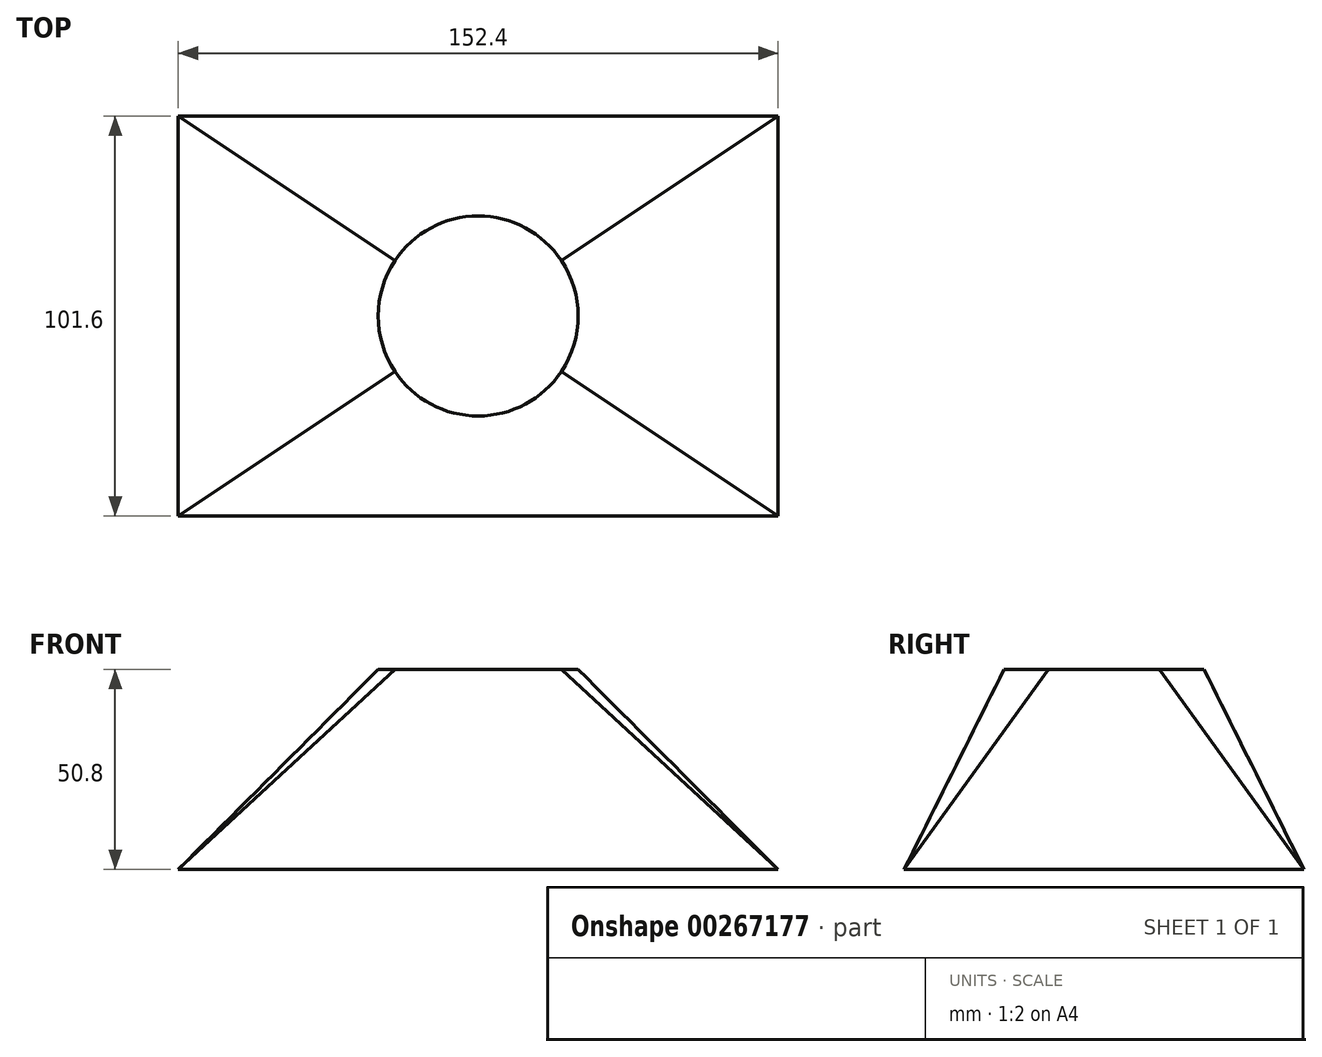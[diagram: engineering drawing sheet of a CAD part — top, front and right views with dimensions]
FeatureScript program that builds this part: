
annotation { "Feature Type Name" : "Feature", "Feature Type Description" : "" }
export const myFeature = defineFeature(function(context is Context, id is Id, definition is map)
    precondition{}
    {
        {
            var Q0;
            Q0=qCreatedBy(makeId("Top.planeOp"),FACE);
            var sketch = newSketch(context, id + "F0", { "sketchPlane" : qUnion([Q0])});
            skLineSegment(sketch, "E0.bottom", {"start": v(76.2, -50.8) * mm, "end": v(-76.2, -50.8) * mm});
            skLineSegment(sketch, "E0.top", {"start": v(76.2, 50.8) * mm, "end": v(-76.2, 50.8) * mm});
            skLineSegment(sketch, "E0.left", {"start": v(76.2, -50.8) * mm, "end": v(76.2, 50.8) * mm});
            skLineSegment(sketch, "E0.right", {"start": v(-76.2, -50.8) * mm, "end": v(-76.2, 50.8) * mm});
            skPoint(sketch, "E0.middle", {"position": v(0, 0) * mm});
            skSolve(sketch);
        }
        {
            var Q0;
            Q0=qCreatedBy(makeId("Top.planeOp"),FACE);
            cPlane(context, id + "F1", {"entities" : qUnion([Q0]), "cplaneType" : CPlaneType.OFFSET, "offset" : 50.8 * mm, "width" : 152.4 * mm, "height" : 152.4 * mm});
        }
        {
            var Q0;
            Q0=qCreatedBy(id+"F1.planeOp",FACE);
            var sketch = newSketch(context, id + "F2", { "sketchPlane" : qUnion([Q0])});
            skPoint(sketch, "E1.0", {"position": v(-76.2, 50.8) * mm});
            skPoint(sketch, "E2.0", {"position": v(76.2, 50.8) * mm});
            skPoint(sketch, "E3.0", {"position": v(76.2, -50.8) * mm});
            skPoint(sketch, "E4.0", {"position": v(-76.2, -50.8) * mm});
            skLineSegment(sketch, "E5", {"start": v(-76.2, 50.8) * mm, "end": v(21.13, -14.09) * mm, "construction": true});
            skLineSegment(sketch, "E6", {"start": v(76.2, 50.8) * mm, "end": v(-76.2, -50.8) * mm, "construction": true});
            skArc(sketch, "E7", {"start": v(-21.13, 14.09) * mm, "mid": v(-25.4, 0) * mm, "end": v(-21.13, -14.09) * mm});
            skArc(sketch, "E8", {"start": v(21.13, 14.09) * mm, "mid": v(0, 25.4) * mm, "end": v(-21.13, 14.09) * mm});
            skLineSegment(sketch, "E9", {"start": v(21.13, -14.09) * mm, "end": v(76.2, -50.8) * mm, "construction": true});
            skArc(sketch, "E10", {"start": v(-21.13, -14.09) * mm, "mid": v(0, -25.4) * mm, "end": v(21.13, -14.09) * mm});
            skArc(sketch, "E11", {"start": v(21.13, -14.09) * mm, "mid": v(25.4, 0) * mm, "end": v(21.13, 14.09) * mm});
            skSolve(sketch);
        }
        {
            var Q0;
            Q0=makeQuery(id+"F0.imprint","IMPRINT",FACE,{"disambiguationData":[TD([[makeQuery(id+"F0.imprint","IMPRINT",EDGE,{"derivedFrom":sQuery(id+"F0.wireOp",EDGE,"E0.bottom")}),-1.0]])]});
            var Q1;
            Q1=makeQuery(id+"F2.imprint","IMPRINT",FACE,{"disambiguationData":[TD([[makeQuery(id+"F2.imprint","IMPRINT",EDGE,{"derivedFrom":sQuery(id+"F2.wireOp",EDGE,"E7")}),1.0]])]});
            loft(context, id + "F3", {"sheetProfilesArray" : [{ "sheetProfileEntities" : qUnion([Q0]) }, { "sheetProfileEntities" : qUnion([Q1]) }]});
        }
    });
